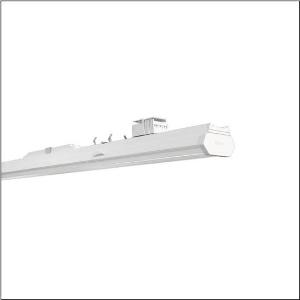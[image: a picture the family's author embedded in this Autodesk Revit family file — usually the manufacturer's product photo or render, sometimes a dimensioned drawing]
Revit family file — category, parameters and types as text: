
# Revit family: licross_r__21_protected_ho_52td12dn4dxm_7c2c
name_source: partatom
category: Lighting Fixtures
units: mm (PartAtom-declared; Revit-internal decimal feet)

## family parameters
Cut with Voids When Loaded = No
Host = Face
Light Source = No
Part Type = Normal
Room Calculation Point = No
Round Connector Dimension = Use Diameter
Shared = No

## types (1)
- --- (1 x LED, 13000 lm, 74.3 W, 4000K)
    Apparent Load = 74 VA
    CIE Flux Codes = 70 91 97 98 100
    Color Rendering = 80
    Color Temperature = 4000K
    Default Elevation = 1800 mm
    Description = Licross® 21 Protected HO, luminaire insert, of sheet steel, galvanised, coil coated, white, length: 1.500mm, width: 90mm, height: 103mm, LED rated luminous flux: 13.000lm, light colour: 840, SDCM (Standard Deviation of Colour Matching)MacAdam ≤ 3 SDCM (initial), control gear: DALI 2, with plug, 5-pole, with phase selection, mains connection: 220..240V, AC, 50/60Hz, rated input power: 74W, internal wiring halogen-free, primary light control with lens, of plastic, primary optical cover: cover, of PMMA, light emission: direct distribution, primary light characteristic: symmetric, protection rating (complete): IP54, insulation class (complete): insulation class I (protective earthing), certification: CE, ENEC, VDE, UKCA, protection symbol: D if used in an environment with non-conductive dust loads with corresponding accessories, impact resistance: IK06, permissible ambient temperature for indoor applications: -25..+40°C, corresponds to IFS (International Featured Standards) requirements for safety and quality in the food industry, reducing of maximum allowable ambient temperature of 5°C with ceiling mounting, LABS conformity tested according to VDMA 24364:2018-05, packaging unit: 1 piece
    Height = 92 mm
    Lamp = 1 x LED
    Lamp Light Flux = 13000 lm
    Lamp Power = 74.3 W
    Lamp count = 1
    Length = 1500 mm
    Luminous efficacy = 175 lm/W
    Manufacturer = Siteco
    ModVariant = No
    Model = 52TD12DN4DXM
    Mounting Place = Ceiling
    Mounting Type = Pendant
    Number of Poles = 1
    OnlyDefault = Yes
    Power Factor = 1
    Product Name = Licross® 21 Protected HO
    Product group = luminaire insert | ceiling pendant
    ProductGroupID = 901
    Protection Class = Protection class I
    Protection Degree = IP 54
    RLX_Detail_Level = 1
    RLX_Emergency_Light_Flux = 0 lm
    RLX_Emergency_Type = 0
    RLX_Emergency_Type_DB = No
    RlxData = <blob elided: 24565 chars, md5=49da2c18>
    Socket = socket
    Standby Power = 0 W
    System Light Flux = 13000 lm
    System Power = 74 W
    Type Comments = factory setting: luminous flux: 100 % | dim-lin: 254 | 424 mA
    Type Image = l_1256148.jpg
    URL = http://relux.com
    VarID = @adj_132877
    Voltage = 0 V
    Weight = 0.00 kg
    Width = 88 mm

## geometry (parser evidence)
native form markers: Blend x4, Sweep x9
no freeform markers — native parametric forms only
